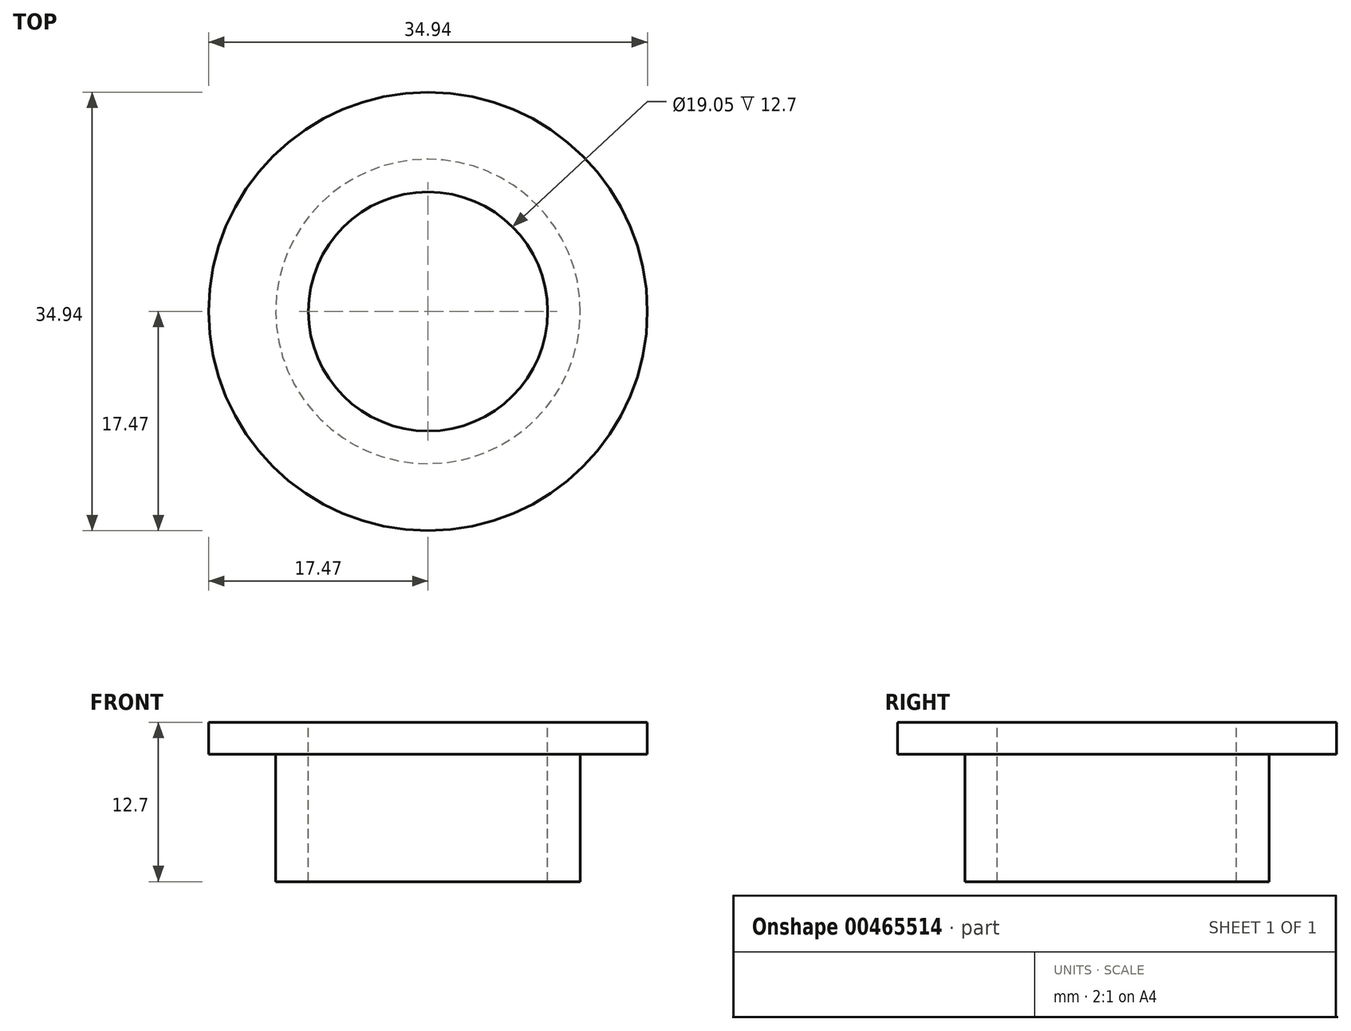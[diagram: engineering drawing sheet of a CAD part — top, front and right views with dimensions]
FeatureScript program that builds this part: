
annotation { "Feature Type Name" : "Feature", "Feature Type Description" : "" }
export const myFeature = defineFeature(function(context is Context, id is Id, definition is map)
    precondition{}
    {
        {
            var Q0;
            Q0=qCreatedBy(makeId("Top.planeOp"),FACE);
            var sketch = newSketch(context, id + "F0", { "sketchPlane" : qUnion([Q0])});
            skCircle(sketch, "E0", {"center": v(0, 0) * mm, "radius": 12.13 * mm});
            skSolve(sketch);
        }
        {
            var Q0;
            Q0=makeQuery(id+"F0.imprint","IMPRINT",FACE,{"disambiguationData":[TD([[makeQuery(id+"F0.imprint","IMPRINT",EDGE,{"derivedFrom":sQuery(id+"F0.wireOp",EDGE,"E0")}),1.0]])]});
            extrude(context, id + "F1", {"entities" : qUnion([Q0]), "depth" : 12.7 * mm});
        }
        {
            var Q0;
            Q0=makeQuery(id+"F1.opExtrude","CAP_FACE",FACE,{"disambiguationData":[OSD([sQuery(id+"F0.wireOp",EDGE,"E0")])],"isStart":false});
            var sketch = newSketch(context, id + "F2", { "sketchPlane" : qUnion([Q0])});
            skCircle(sketch, "E1", {"center": v(0, 0) * mm, "radius": 9.53 * mm});
            skCircle(sketch, "E2", {"center": v(0, 0) * mm, "radius": 17.47 * mm});
            skSolve(sketch);
        }
        {
            var Q0;
            Q0=makeQuery(id+"F2.imprint","IMPRINT",FACE,{"disambiguationData":[TD([[makeQuery(id+"F2.imprint","IMPRINT",EDGE,{"derivedFrom":sQuery(id+"F2.wireOp",EDGE,"E1")}),1.0]])]});
            extrude(context, id + "F3", {"entities" : qUnion([Q0]), "operationType" : NewBodyOperationType.REMOVE, "endBound" : BoundingType.THROUGH_ALL, "oppositeDirection" : true, "depth" : 25.4 * mm});
        }
        {
            var Q0;
            Q0=makeQuery(id+"F2.imprint","IMPRINT",FACE,{"disambiguationData":[TD([[makeQuery(id+"F2.imprint","IMPRINT",EDGE,{"derivedFrom":sQuery(id+"F2.wireOp",EDGE,"E2")}),1.0]])]});
            extrude(context, id + "F4", {"entities" : qUnion([Q0]), "operationType" : NewBodyOperationType.ADD, "oppositeDirection" : true, "depth" : 2.54 * mm});
        }
    });
